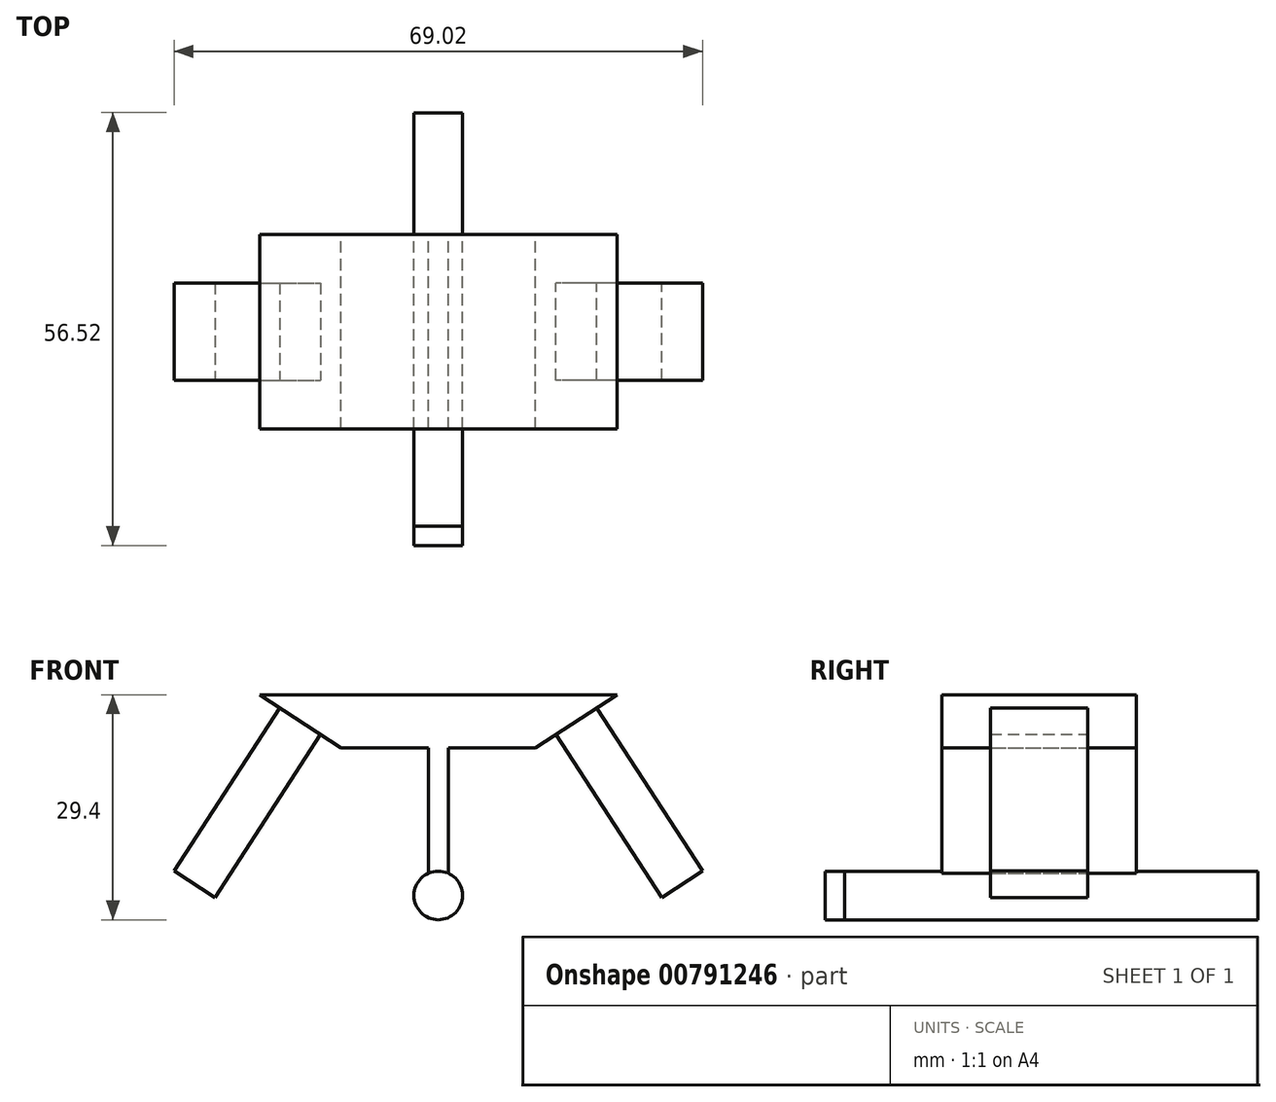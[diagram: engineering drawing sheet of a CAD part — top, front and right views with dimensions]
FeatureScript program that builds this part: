
annotation { "Feature Type Name" : "Feature", "Feature Type Description" : "" }
export const myFeature = defineFeature(function(context is Context, id is Id, definition is map)
    precondition{}
    {
        {
            var Q0;
            Q0=qCreatedBy(makeId("Front.planeOp"),FACE);
            var sketch = newSketch(context, id + "F0", { "sketchPlane" : qUnion([Q0])});
            skLineSegment(sketch, "E0", {"start": v(1.31, 19.3) * mm, "end": v(12.7, 19.3) * mm});
            skLineSegment(sketch, "E1", {"start": v(-1.31, 19.3) * mm, "end": v(-12.7, 19.3) * mm});
            skLineSegment(sketch, "E2", {"start": v(-12.7, 19.3) * mm, "end": v(-23.34, 26.22) * mm});
            skLineSegment(sketch, "E3.MirrorCS", {"start": v(12.7, 19.3) * mm, "end": v(23.34, 26.22) * mm});
            skCircle(sketch, "E4", {"center": v(0, 0) * mm, "radius": 3.18 * mm});
            skLineSegment(sketch, "E5", {"start": v(-1.31, 2.9) * mm, "end": v(-1.31, 19.3) * mm});
            skLineSegment(sketch, "E6.MirrorCS", {"start": v(1.31, 2.9) * mm, "end": v(1.31, 19.3) * mm});
            skLineSegment(sketch, "E7", {"start": v(23.34, 26.22) * mm, "end": v(-23.34, 26.22) * mm});
            skSolve(sketch);
        }
        {
            var Q0;
            Q0 = qSketchRegion(id + "F0", true);
            extrude(context, id + "F1", {"entities" : qUnion([Q0]), "depth" : 25.4 * mm, "offsetDistance" : 25.4 * mm});
        }
        {
            var Q0;
            Q0=makeQuery(id+"F1.opExtrude","CAP_FACE",FACE,{"disambiguationData":[OSD([sQuery(id+"F0.wireOp",EDGE,"E0"),sQuery(id+"F0.wireOp",EDGE,"E1"),sQuery(id+"F0.wireOp",EDGE,"E2"),sQuery(id+"F0.wireOp",EDGE,"E3.MirrorCS"),sQuery(id+"F0.wireOp",EDGE,"IWLkmbKA-51x1-fiLq-LZ8A-FQyaZecVXL8N"),sQuery(id+"F0.wireOp",EDGE,"XXaJP8mJ-kF1p-upIE-9jIi-1xHyME5rrbFG"),sQuery(id+"F0.wireOp",EDGE,"E4"),sQuery(id+"F0.wireOp",EDGE,"E5"),sQuery(id+"F0.wireOp",EDGE,"E6.MirrorCS")])],"isStart":false});
            var sketch = newSketch(context, id + "F2", { "sketchPlane" : qUnion([Q0])});
            skCircle(sketch, "E8", {"center": v(0, 0) * mm, "radius": 3.17 * mm});
            skSolve(sketch);
        }
        {
            var Q0;
            Q0 = qSketchRegion(id + "F2", true);
            extrude(context, id + "F3", {"entities" : qUnion([Q0]), "operationType" : NewBodyOperationType.ADD, "depth" : 12.7 * mm, "offsetDistance" : 25.4 * mm});
        }
        {
            var Q0;
            Q0=makeQuery(id+"F1.opExtrude","CAP_FACE",FACE,{"disambiguationData":[OSD([sQuery(id+"F0.wireOp",EDGE,"E0"),sQuery(id+"F0.wireOp",EDGE,"E1"),sQuery(id+"F0.wireOp",EDGE,"E2"),sQuery(id+"F0.wireOp",EDGE,"E3.MirrorCS"),sQuery(id+"F0.wireOp",EDGE,"IWLkmbKA-51x1-fiLq-LZ8A-FQyaZecVXL8N"),sQuery(id+"F0.wireOp",EDGE,"XXaJP8mJ-kF1p-upIE-9jIi-1xHyME5rrbFG"),sQuery(id+"F0.wireOp",EDGE,"E4"),sQuery(id+"F0.wireOp",EDGE,"E5"),sQuery(id+"F0.wireOp",EDGE,"E6.MirrorCS")])],"isStart":true});
            var sketch = newSketch(context, id + "F4", { "sketchPlane" : qUnion([Q0])});
            skCircle(sketch, "E9", {"center": v(0, 0) * mm, "radius": 3.18 * mm});
            skSolve(sketch);
        }
        {
            var Q0;
            Q0 = qSketchRegion(id + "F4", true);
            extrude(context, id + "F5", {"entities" : qUnion([Q0]), "operationType" : NewBodyOperationType.ADD, "depth" : 12.7 * mm, "offsetDistance" : 25.4 * mm});
        }
        {
            var Q0;
            Q0=makeQuery(id+"F3.opExtrude","CAP_FACE",FACE,{"disambiguationData":[OSD([sQuery(id+"F2.wireOp",EDGE,"E8")])],"isStart":false});
            extrude(context, id + "F6", {"entities" : qUnion([Q0]), "depth" : 2.54 * mm, "offsetDistance" : 25.4 * mm});
        }
        {
            var Q0;
            Q0=makeQuery(id+"F5.opExtrude","CAP_FACE",FACE,{"disambiguationData":[OSD([sQuery(id+"F4.wireOp",EDGE,"E9")])],"isStart":false});
            extrude(context, id + "F7", {"entities" : qUnion([Q0]), "operationType" : NewBodyOperationType.ADD, "depth" : 3.17 * mm, "offsetDistance" : 25.4 * mm});
        }
        {
            var Q0;
            Q0=makeQuery(id+"F1.opExtrude","SWEPT_FACE",FACE,{"disambiguationData":[OSD([sQuery(id+"F0.wireOp",EDGE,"E3.MirrorCS")])]});
            var sketch = newSketch(context, id + "F8", { "sketchPlane" : qUnion([Q0])});
            skLineSegment(sketch, "E10.bottom", {"start": v(30.68, 19.05) * mm, "end": v(24.33, 19.05) * mm});
            skLineSegment(sketch, "E10.top", {"start": v(30.68, 6.35) * mm, "end": v(24.33, 6.35) * mm});
            skLineSegment(sketch, "E10.left", {"start": v(30.68, 19.05) * mm, "end": v(30.68, 6.35) * mm});
            skLineSegment(sketch, "E10.right", {"start": v(24.33, 19.05) * mm, "end": v(24.33, 6.35) * mm});
            skSolve(sketch);
        }
        {
            var Q0;
            Q0=makeQuery(id+"F8.imprint","IMPRINT",FACE,{"disambiguationData":[TD([[makeQuery(id+"F8.imprint","IMPRINT",EDGE,{"derivedFrom":sQuery(id+"F8.wireOp",EDGE,"E10.bottom")}),1.0]])]});
            extrude(context, id + "F9", {"entities" : qUnion([Q0]), "operationType" : NewBodyOperationType.ADD, "depth" : 25.4 * mm, "offsetDistance" : 25.4 * mm});
        }
        {
            var Q0;
            Q0=makeQuery(id+"F1.opExtrude","SWEPT_FACE",FACE,{"disambiguationData":[OSD([sQuery(id+"F0.wireOp",EDGE,"E2")])]});
            var sketch = newSketch(context, id + "F10", { "sketchPlane" : qUnion([Q0])});
            skLineSegment(sketch, "E11.bottom", {"start": v(-30.68, 6.35) * mm, "end": v(-24.33, 6.35) * mm});
            skLineSegment(sketch, "E11.top", {"start": v(-30.68, 19.05) * mm, "end": v(-24.33, 19.05) * mm});
            skLineSegment(sketch, "E11.left", {"start": v(-30.68, 6.35) * mm, "end": v(-30.68, 19.05) * mm});
            skLineSegment(sketch, "E11.right", {"start": v(-24.33, 6.35) * mm, "end": v(-24.33, 19.05) * mm});
            skSolve(sketch);
        }
        {
            var Q0;
            Q0=makeQuery(id+"F10.imprint","IMPRINT",FACE,{"disambiguationData":[TD([[makeQuery(id+"F10.imprint","IMPRINT",EDGE,{"derivedFrom":sQuery(id+"F10.wireOp",EDGE,"E11.bottom")}),1.0]])]});
            extrude(context, id + "F11", {"entities" : qUnion([Q0]), "operationType" : NewBodyOperationType.ADD, "depth" : 25.4 * mm, "offsetDistance" : 25.4 * mm});
        }
    });
